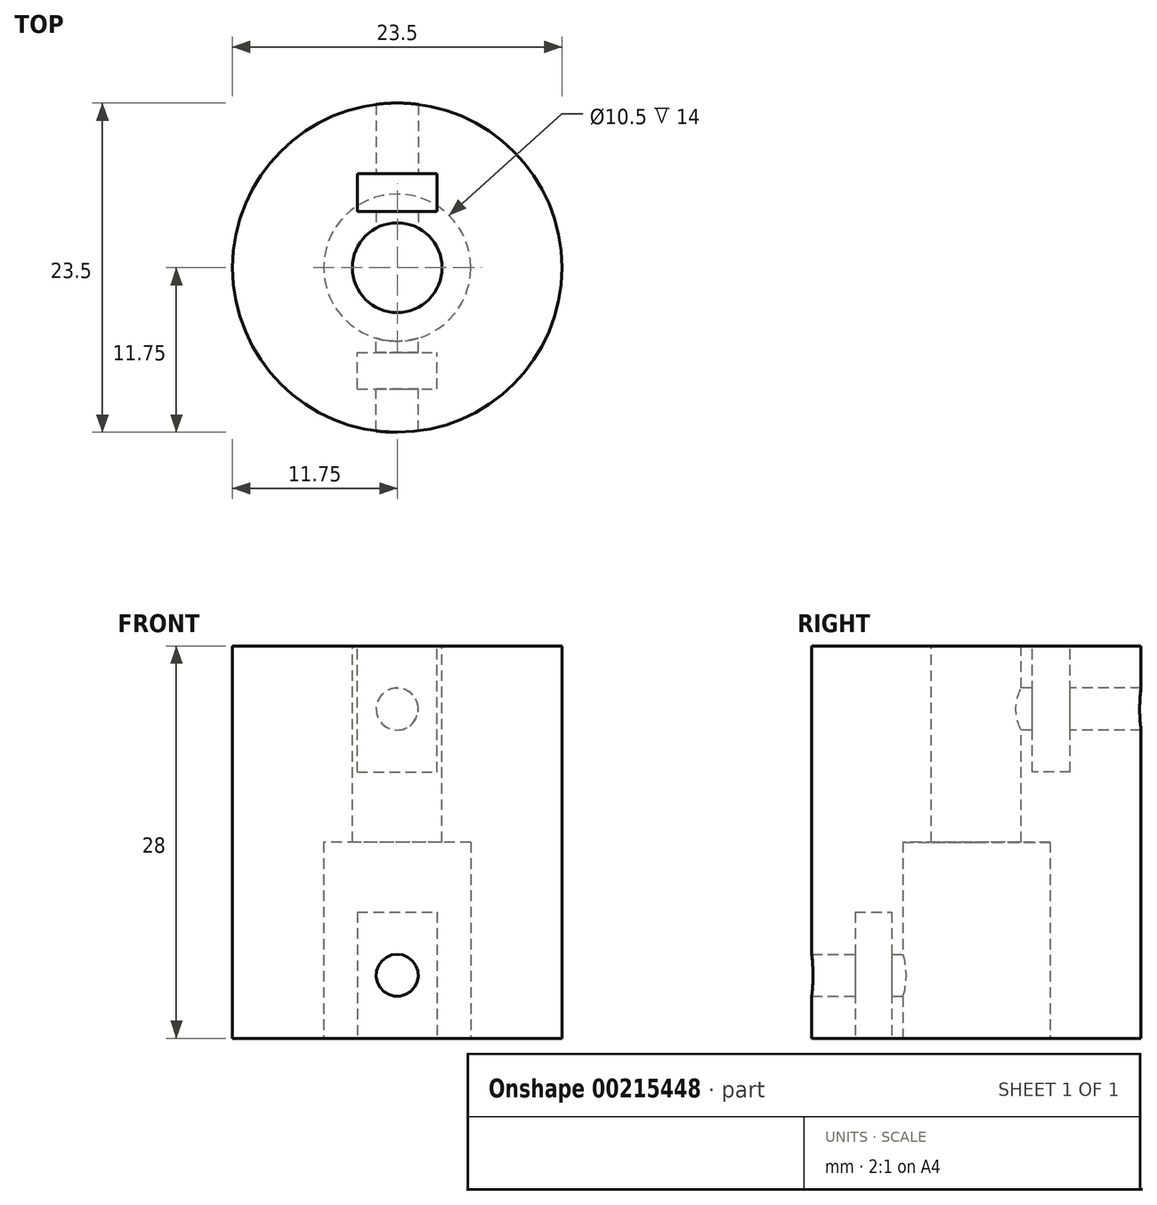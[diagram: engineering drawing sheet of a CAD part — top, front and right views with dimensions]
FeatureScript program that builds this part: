
annotation { "Feature Type Name" : "Feature", "Feature Type Description" : "" }
export const myFeature = defineFeature(function(context is Context, id is Id, definition is map)
    precondition{}
    {
        {
            var Q0;
            Q0=qCreatedBy(makeId("Top.planeOp"),FACE);
            var sketch = newSketch(context, id + "F0", { "sketchPlane" : qUnion([Q0])});
            skCircle(sketch, "E0", {"center": v(0, 0) * mm, "radius": 11.75 * mm});
            skSolve(sketch);
        }
        {
            var Q0;
            Q0=qCreatedBy(makeId("Top.planeOp"),FACE);
            cPlane(context, id + "F1", {"entities" : qUnion([Q0]), "cplaneType" : CPlaneType.OFFSET, "offset" : 28 * mm, "width" : 150 * mm, "height" : 150 * mm});
        }
        {
            var Q0;
            Q0=qCreatedBy(id+"F1.planeOp",FACE);
            var sketch = newSketch(context, id + "F2", { "sketchPlane" : qUnion([Q0])});
            skCircle(sketch, "E1", {"center": v(0, 0) * mm, "radius": 3.2 * mm});
            skCircle(sketch, "E2", {"center": v(0, 0) * mm, "radius": 11.75 * mm});
            skSolve(sketch);
        }
        {
            var Q0;
            Q0 = qSketchRegion(id + "F0", true);
            extrude(context, id + "F3", {"entities" : qUnion([Q0]), "depth" : 28 * mm});
        }
        {
            var Q0;
            Q0=qCreatedBy(makeId("Top.planeOp"),FACE);
            var sketch = newSketch(context, id + "F4", { "sketchPlane" : qUnion([Q0])});
            skCircle(sketch, "E3", {"center": v(0, 0) * mm, "radius": 5.25 * mm});
            skSolve(sketch);
        }
        {
            var Q0;
            Q0 = qSketchRegion(id + "F4", true);
            extrude(context, id + "F5", {"entities" : qUnion([Q0]), "operationType" : NewBodyOperationType.REMOVE, "depth" : 14 * mm});
        }
        {
            var Q0;
            Q0=makeQuery(id+"F2.imprint","IMPRINT",FACE,{"disambiguationData":[TD([[makeQuery(id+"F2.imprint","IMPRINT",EDGE,{"derivedFrom":sQuery(id+"F2.wireOp",EDGE,"E1")}),1.0]])]});
            var Q1;
            Q1=sQuery(id+"F2.wireOp",EDGE,"E1");
            extrude(context, id + "F6", {"entities" : qUnion([Q0]), "operationType" : NewBodyOperationType.REMOVE, "surfaceEntities" : qUnion([Q1]), "oppositeDirection" : true, "depth" : 14 * mm});
        }
        {
            var Q0;
            Q0=qCreatedBy(id+"F1.planeOp",FACE);
            var sketch = newSketch(context, id + "F7", { "sketchPlane" : qUnion([Q0])});
            skLineSegment(sketch, "E4.bottom", {"start": v(-2.85, 6.7) * mm, "end": v(2.85, 6.7) * mm});
            skLineSegment(sketch, "E4.top", {"start": v(-2.85, 4) * mm, "end": v(2.85, 4) * mm});
            skLineSegment(sketch, "E4.left", {"start": v(-2.85, 6.7) * mm, "end": v(-2.85, 4) * mm});
            skLineSegment(sketch, "E4.right", {"start": v(2.85, 6.7) * mm, "end": v(2.85, 4) * mm});
            skSolve(sketch);
        }
        {
            var Q0;
            Q0=makeQuery(id+"F7.imprint","IMPRINT",FACE,{"disambiguationData":[TD([[makeQuery(id+"F7.imprint","IMPRINT",EDGE,{"derivedFrom":sQuery(id+"F7.wireOp",EDGE,"E4.bottom")}),-1.0]])]});
            extrude(context, id + "F8", {"entities" : qUnion([Q0]), "operationType" : NewBodyOperationType.REMOVE, "oppositeDirection" : true, "depth" : 9 * mm});
        }
        {
            var Q0;
            Q0=qCreatedBy(makeId("Top.planeOp"),FACE);
            var sketch = newSketch(context, id + "F9", { "sketchPlane" : qUnion([Q0])});
            skLineSegment(sketch, "E5.bottom", {"start": v(-2.85, -8.65) * mm, "end": v(2.85, -8.65) * mm});
            skLineSegment(sketch, "E5.top", {"start": v(-2.85, -6.05) * mm, "end": v(2.85, -6.05) * mm});
            skLineSegment(sketch, "E5.left", {"start": v(-2.85, -8.65) * mm, "end": v(-2.85, -6.05) * mm});
            skLineSegment(sketch, "E5.right", {"start": v(2.85, -8.65) * mm, "end": v(2.85, -6.05) * mm});
            skSolve(sketch);
        }
        {
            var Q0;
            Q0=makeQuery(id+"F9.imprint","IMPRINT",FACE,{"disambiguationData":[TD([[makeQuery(id+"F9.imprint","IMPRINT",EDGE,{"derivedFrom":sQuery(id+"F9.wireOp",EDGE,"E5.bottom")}),1.0]])]});
            extrude(context, id + "F10", {"entities" : qUnion([Q0]), "operationType" : NewBodyOperationType.REMOVE, "depth" : 9 * mm});
        }
        {
            var Q0;
            Q0=qCreatedBy(makeId("Front.planeOp"),FACE);
            var sketch = newSketch(context, id + "F11", { "sketchPlane" : qUnion([Q0])});
            skCircle(sketch, "E6", {"center": v(0, 4.5) * mm, "radius": 1.5 * mm});
            skSolve(sketch);
        }
        {
            var Q0;
            Q0 = qSketchRegion(id + "F11", true);
            extrude(context, id + "F12", {"entities" : qUnion([Q0]), "operationType" : NewBodyOperationType.REMOVE, "depth" : 25 * mm});
        }
        {
            var Q0;
            Q0=qCreatedBy(makeId("Front.planeOp"),FACE);
            var sketch = newSketch(context, id + "F13", { "sketchPlane" : qUnion([Q0])});
            skCircle(sketch, "E7", {"center": v(0, 23.5) * mm, "radius": 1.5 * mm});
            skSolve(sketch);
        }
        {
            var Q0;
            Q0 = qSketchRegion(id + "F13", true);
            extrude(context, id + "F14", {"entities" : qUnion([Q0]), "operationType" : NewBodyOperationType.REMOVE, "oppositeDirection" : true, "depth" : 25 * mm});
        }
    });
